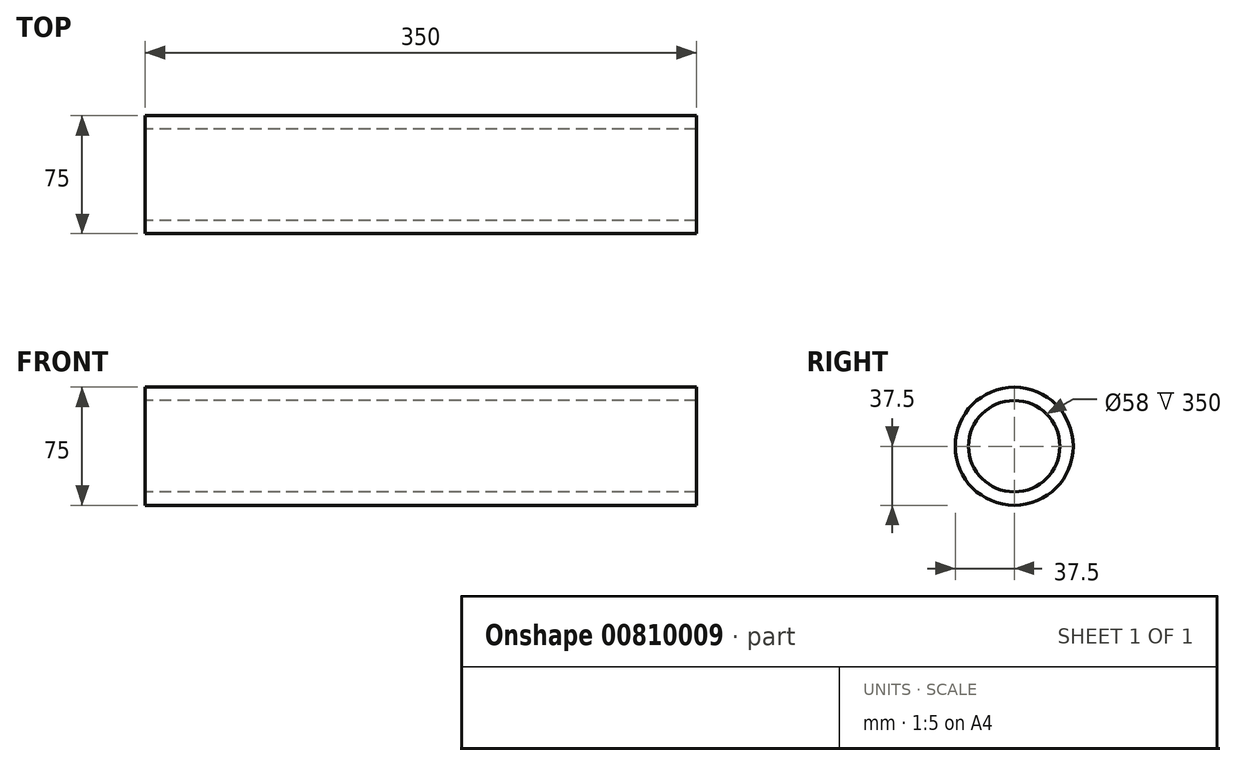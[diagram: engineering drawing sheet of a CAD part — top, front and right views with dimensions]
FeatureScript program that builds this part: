
annotation { "Feature Type Name" : "Feature", "Feature Type Description" : "" }
export const myFeature = defineFeature(function(context is Context, id is Id, definition is map)
    precondition{}
    {
        {
            var Q0;
            Q0=qCreatedBy(makeId("Right.planeOp"),FACE);
            var sketch = newSketch(context, id + "F0", { "sketchPlane" : qUnion([Q0])});
            skCircle(sketch, "E0", {"center": v(0, 0) * mm, "radius": 37.5 * mm});
            skCircle(sketch, "E1", {"center": v(0, 0) * mm, "radius": 29 * mm});
            skSolve(sketch);
        }
        {
            var Q0;
            Q0 = qSketchRegion(id + "F0", true);
            extrude(context, id + "F1", {"entities" : qUnion([Q0]), "endBound" : BoundingType.SYMMETRIC, "depth" : 350 * mm, "offsetDistance" : 25 * mm});
        }
    });
